# Revit family: DVS
name_source: partatom
category: Wyposażenie mechaniczne
revit_build: Autodesk Revit 2017 (Build: 20160225_1515(x64)
units: mm (PartAtom-declared; Revit-internal decimal feet)

## family parameters
Oparty na płaszczyźnie roboczej = Nie
Punkt obliczania pomieszczeń = Nie
Tnij formami wycięć po wczytaniu = Nie
Typ części = Normalny
Współdzielony = Nie
Wymiar okrągłego złącza = Użyj średnicy
Zawsze pionowo = Tak

## types (32) — shared parameters
Date = 01.2019
Frequency = 50 Hz
Producent = Rosenberg
Text_1 = 340 mm
Text_2 = 170 mm
URL = https://www.rosenberg.pl
Version = 1

## per-type parameters (varying)
| type | A | Air_flow | Current | Da | Di | H | Height | L | P | Power | Pressure | Protection_class | Text_size | Voltage | Weight[kg] | Width | Width_bottom | max.Ambient_temperature | t1 |
| 190-2 E.3BE | 294 mm  [stored 0.964567 ft] | 291.0 m³/h | 0 A | 235 mm  [stored 0.770997 ft] | 186 mm  [stored 0.610236 ft] | 600 mm | 290 mm  [stored 0.951444 ft] | 115 mm  [stored 0.377297 ft] | 571 mm  [stored 1.87336 ft] | 0 kW | 199.0 Pa | IP44 | 15 mm  [stored 0.0492126 ft] | 230 V | 22 | 540 mm  [stored 1.77165 ft] | 335 mm  [stored 1.09908 ft] | 70 °C | 2 mm  [stored 0.00656168 ft] |
| 225-2 E.3CF | 294 mm  [stored 0.964567 ft] | 449.0 m³/h | 0 A | 235 mm  [stored 0.770997 ft] | 186 mm  [stored 0.610236 ft] | 600 mm | 290 mm  [stored 0.951444 ft] | 115 mm  [stored 0.377297 ft] | 571 mm  [stored 1.87336 ft] | 0 kW | 218.0 Pa | IP44 | 20 mm  [stored 0.0656168 ft] | 230 V | 9 | 540 mm  [stored 1.77165 ft] | 335 mm  [stored 1.09908 ft] | 70 °C | 2 mm  [stored 0.00656168 ft] |
| 280-2 E.3EF V1 | 395 mm  [stored 1.29593 ft] | 839.0 m³/h | 1 A | 306 mm  [stored 1.00394 ft] | 256 mm  [stored 0.839895 ft] | 700 mm | 390 mm  [stored 1.27953 ft] | 156 mm  [stored 0.511811 ft] | 657 mm | 0 kW | 381.0 Pa | IP44 | 25 mm  [stored 0.082021 ft] | 230 V | 22.5 | 720 mm | 435 mm  [stored 1.42717 ft] | 70 °C | 2 mm  [stored 0.00656168 ft] |
| 310-4 E.3EF | 395 mm  [stored 1.29593 ft] | 1031.0 m³/h | 1 A | 306 mm  [stored 1.00394 ft] | 256 mm  [stored 0.839895 ft] | 700 mm | 390 mm  [stored 1.27953 ft] | 156 mm  [stored 0.511811 ft] | 657 mm | 0 kW | 133.0 Pa | IP44 | 25 mm  [stored 0.082021 ft] | 230 V | 22 | 720 mm | 435 mm  [stored 1.42717 ft] | 70 °C | 2 mm  [stored 0.00656168 ft] |
| 355-4 E.5FA | 555 mm  [stored 1.82087 ft] | 1639.0 m³/h | 1 A | 464 mm  [stored 1.52231 ft] | 402 mm  [stored 1.3189 ft] | 900 mm | 445 mm  [stored 1.45997 ft] | 220 mm  [stored 0.721785 ft] | 817 mm | 0 kW | 278.0 Pa | IP54 | 30 mm  [stored 0.0984252 ft] | 230 V | 34 | 915 mm | 595 mm  [stored 1.9521 ft] | 70 °C | 2 mm  [stored 0.00656168 ft] |
| 400-4 E.5HA | 555 mm  [stored 1.82087 ft] | 2411.0 m³/h | 3 A | 464 mm  [stored 1.52231 ft] | 402 mm  [stored 1.3189 ft] | 900 mm | 445 mm  [stored 1.45997 ft] | 220 mm  [stored 0.721785 ft] | 817 mm | 1 kW | 330.0 Pa | IP54 | 35 mm  [stored 0.114829 ft] | 230 V | 34 | 915 mm | 595 mm  [stored 1.9521 ft] | 65 °C | 2 mm  [stored 0.00656168 ft] |
| 450-4 E.6FA | 625 mm | 3424.0 m³/h | 4 A | 464 mm  [stored 1.52231 ft] | 402 mm  [stored 1.3189 ft] | 900 mm | 480 mm  [stored 1.5748 ft] | 220 mm  [stored 0.721785 ft] | 877 mm | 1 kW | 448.0 Pa | IP54 | 40 mm  [stored 0.131234 ft] | 230 V | 46.2 | 1005 mm | 665 mm | 45 °C | 2 mm  [stored 0.00656168 ft] |
| 500-4 E.6HF | 625 mm | 4745.0 m³/h | 6 A | 464 mm  [stored 1.52231 ft] | 402 mm  [stored 1.3189 ft] | 900 mm | 480 mm  [stored 1.5748 ft] | 220 mm  [stored 0.721785 ft] | 877 mm | 1 kW | 509.0 Pa | IP54 | 50 mm  [stored 0.164042 ft] | 230 V | 54 | 1005 mm | 665 mm | 40 °C | 2 mm  [stored 0.00656168 ft] |
| 560-4 D Zone 1 | 895 mm | 0.0 m³/h | 5 A | 639 mm | 569 mm  [stored 1.8668 ft] | 1070 mm | 520 mm  [stored 1.70604 ft] | 255 mm  [stored 0.836614 ft] | 1200 mm | 2 kW | 0.0 Pa | IP44 | 50 mm  [stored 0.164042 ft] | 400 V | 68 | 1150 mm | 939 mm | 40 °C | 2 mm  [stored 0.00656168 ft] |
| 630-4 D.7KF | 895 mm | 9404.0 m³/h | 6 A | 639 mm | 569 mm  [stored 1.8668 ft] | 1070 mm | 600 mm | 255 mm  [stored 0.836614 ft] | 1200 mm | 4 kW | 718.0 Pa | IP54 | 50 mm  [stored 0.164042 ft] | 400 V | 94 | 1405 mm | 939 mm | 40 °C | 2 mm  [stored 0.00656168 ft] |
| 710-6 D.7NA | 985 mm | 8203.0 m³/h | 5 A | 708 mm | 635 mm | 1160 mm | 700 mm | 250 mm  [stored 0.82021 ft] | 1300 mm | 2 kW | 479.0 Pa | IP54 | 50 mm  [stored 0.164042 ft] | 400 V | 115 | 1510 mm | 1035 mm | 70 °C | 4 mm  [stored 0.0131234 ft] |
| 280-4 E.3EF | 395 mm  [stored 1.29593 ft] | 674.0 m³/h | 0 A | 306 mm  [stored 1.00394 ft] | 256 mm  [stored 0.839895 ft] | 700 mm | 390 mm  [stored 1.27953 ft] | 156 mm  [stored 0.511811 ft] | 657 mm | 0 kW | 129.0 Pa | IP44 | 25 mm  [stored 0.082021 ft] | 230 V | 9.5 | 720 mm | 435 mm  [stored 1.42717 ft] | 70 °C | 2 mm  [stored 0.00656168 ft] |
| 310-4 D.3EF | 395 mm  [stored 1.29593 ft] | 929.0 m³/h | 0 A | 306 mm  [stored 1.00394 ft] | 256 mm  [stored 0.839895 ft] | 700 mm | 390 mm  [stored 1.27953 ft] | 156 mm  [stored 0.511811 ft] | 657 mm | 0 kW | 117.0 Pa | IP54 | 25 mm  [stored 0.082021 ft] | 400 V | 22 | 720 mm | 435 mm  [stored 1.42717 ft] | 70 °C | 2 mm  [stored 0.00656168 ft] |
| 355-4 D.5DF | 555 mm  [stored 1.82087 ft] | 1693.0 m³/h | 1 A | 464 mm  [stored 1.52231 ft] | 402 mm  [stored 1.3189 ft] | 900 mm | 445 mm  [stored 1.45997 ft] | 220 mm  [stored 0.721785 ft] | 817 mm | 0 kW | 266.0 Pa | IP54 | 30 mm  [stored 0.0984252 ft] | 230 V | 25 | 915 mm | 595 mm  [stored 1.9521 ft] | 70 °C | 2 mm  [stored 0.00656168 ft] |
| 400-4 D.5FA | 555 mm  [stored 1.82087 ft] | 2470.0 m³/h | 1 A | 464 mm  [stored 1.52231 ft] | 402 mm  [stored 1.3189 ft] | 900 mm | 445 mm  [stored 1.45997 ft] | 220 mm  [stored 0.721785 ft] | 817 mm | 0 kW | 299.0 Pa | IP54 | 35 mm  [stored 0.114829 ft] | 400 V | 32 | 915 mm | 595 mm  [stored 1.9521 ft] | 70 °C | 2 mm  [stored 0.00656168 ft] |
| 450-4 D.5HA | 625 mm | 3385.0 m³/h | 2 A | 464 mm  [stored 1.52231 ft] | 402 mm  [stored 1.3189 ft] | 900 mm | 480 mm  [stored 1.5748 ft] | 220 mm  [stored 0.721785 ft] | 877 mm | 1 kW | 393.0 Pa | IP54 | 40 mm  [stored 0.131234 ft] | 400 V | 43.5 | 1005 mm | 665 mm | 55 °C | 2 mm  [stored 0.00656168 ft] |
| 450-6 D.5HA | 625 mm | 2289.0 m³/h | 1 A | 464 mm  [stored 1.52231 ft] | 402 mm  [stored 1.3189 ft] | 900 mm | 480 mm  [stored 1.5748 ft] | 220 mm  [stored 0.721785 ft] | 877 mm | 0 kW | 178.0 Pa | IP54 | 40 mm  [stored 0.131234 ft] | 400 V | 43.5 | 1005 mm | 665 mm | 60 °C | 2 mm  [stored 0.00656168 ft] |
| 500-4 D.6HF | 625 mm | 4635.0 m³/h | 3 A | 464 mm  [stored 1.52231 ft] | 402 mm  [stored 1.3189 ft] | 900 mm | 480 mm  [stored 1.5748 ft] | 220 mm  [stored 0.721785 ft] | 877 mm | 1 kW | 527.0 Pa | IP54 | 50 mm  [stored 0.164042 ft] | 400 V | 53 | 1005 mm | 665 mm | 70 °C | 2 mm  [stored 0.00656168 ft] |
| 500-6 D.6DF | 625 mm | 3114.0 m³/h | 1 A | 464 mm  [stored 1.52231 ft] | 402 mm  [stored 1.3189 ft] | 900 mm | 480 mm  [stored 1.5748 ft] | 220 mm  [stored 0.721785 ft] | 877 mm | 0 kW | 221.0 Pa | IP54 | 50 mm  [stored 0.164042 ft] | 400 V | 53 | 1005 mm | 665 mm | 65 °C | 2 mm  [stored 0.00656168 ft] |
| 560-6 D.6FA | 895 mm | 4452.0 m³/h | 2 A | 639 mm | 569 mm  [stored 1.8668 ft] | 1070 mm | 600 mm | 255 mm  [stored 0.836614 ft] | 1200 mm | 1 kW | 267.0 Pa | IP54 | 50 mm  [stored 0.164042 ft] | 400 V | 77 | 1405 mm | 939 mm | 50 °C | 2 mm  [stored 0.00656168 ft] |
| 630-6 D.6LA | 895 mm | 5181.0 m³/h | 3 A | 639 mm | 569 mm  [stored 1.8668 ft] | 1070 mm | 600 mm | 255 mm  [stored 0.836614 ft] | 1200 mm | 1 kW | 418.0 Pa | IP54 | 50 mm  [stored 0.164042 ft] | 400 V | 83 | 1405 mm | 939 mm | 65 °C | 2 mm  [stored 0.00656168 ft] |
| 800-6 KD.7NA | 985 mm | 10571.0 m³/h | 6 A | 708 mm | 635 mm | 1160 mm | 700 mm | 250 mm  [stored 0.82021 ft] | 1300 mm | 3 kW | 572.0 Pa | IP54 | 50 mm  [stored 0.164042 ft] | 400 V | 172 | 1510 mm | 1035 mm | 50 °C | 4 mm  [stored 0.0131234 ft] |
| 310 K-4 D Zone 2 | 395 mm  [stored 1.29593 ft] | 0.0 m³/h | 0 A | 306 mm  [stored 1.00394 ft] | 256 mm  [stored 0.839895 ft] | 700 mm | 350 mm  [stored 1.14829 ft] | 156 mm  [stored 0.511811 ft] | 657 mm | 0 kW | 0.0 Pa | IP44 | 25 mm  [stored 0.082021 ft] | 400 V | 22 | 560 mm  [stored 1.83727 ft] | 435 mm  [stored 1.42717 ft] | 40 °C | 2 mm  [stored 0.00656168 ft] |
| 310 L-4 D Zone 2 | 395 mm  [stored 1.29593 ft] | 0.0 m³/h | 0 A | 306 mm  [stored 1.00394 ft] | 256 mm  [stored 0.839895 ft] | 700 mm | 350 mm  [stored 1.14829 ft] | 156 mm  [stored 0.511811 ft] | 657 mm | 0 kW | 0.0 Pa | IP44 | 25 mm  [stored 0.082021 ft] | 400 V | 21.5 | 560 mm  [stored 1.83727 ft] | 435 mm  [stored 1.42717 ft] | 40 °C | 2 mm  [stored 0.00656168 ft] |
| 355-4 D Zone 1 | 555 mm  [stored 1.82087 ft] | 0.0 m³/h | 1 A | 464 mm  [stored 1.52231 ft] | 402 mm  [stored 1.3189 ft] | 900 mm | 445 mm  [stored 1.45997 ft] | 220 mm  [stored 0.721785 ft] | 817 mm | 0 kW | 0.0 Pa | IP44 | 30 mm  [stored 0.0984252 ft] | 400 V | 32 | 915 mm | 595 mm  [stored 1.9521 ft] | 40 °C | 2 mm  [stored 0.00656168 ft] |
| 355-4 D Zone 2 | 555 mm  [stored 1.82087 ft] | 0.0 m³/h | 1 A | 464 mm  [stored 1.52231 ft] | 402 mm  [stored 1.3189 ft] | 900 mm | 445 mm  [stored 1.45997 ft] | 220 mm  [stored 0.721785 ft] | 817 mm | 0 kW | 0.0 Pa | IP44 | 30 mm  [stored 0.0984252 ft] | 400 V | 32 | 915 mm | 595 mm  [stored 1.9521 ft] | 40 °C | 2 mm  [stored 0.00656168 ft] |
| 400-4 D Zone 2 | 555 mm  [stored 1.82087 ft] | 0.0 m³/h | 1 A | 464 mm  [stored 1.52231 ft] | 402 mm  [stored 1.3189 ft] | 900 mm | 445 mm  [stored 1.45997 ft] | 220 mm  [stored 0.721785 ft] | 817 mm | 0 kW | 0.0 Pa | IP44 | 35 mm  [stored 0.114829 ft] | 400 V | 24.5 | 915 mm | 595 mm  [stored 1.9521 ft] | 40 °C | 2 mm  [stored 0.00656168 ft] |
| 450-4 D Zone 1 | 625 mm | 0.0 m³/h | 1 A | 464 mm  [stored 1.52231 ft] | 402 mm  [stored 1.3189 ft] | 900 mm | 450 mm  [stored 1.47638 ft] | 220 mm  [stored 0.721785 ft] | 877 mm | 1 kW | 0.0 Pa | IP44 | 40 mm  [stored 0.131234 ft] | 400 V | 43.5 | 900 mm | 665 mm | 40 °C | 2 mm  [stored 0.00656168 ft] |
| 450-4 D Zone 2 | 625 mm | 0.0 m³/h | 1 A | 464 mm  [stored 1.52231 ft] | 402 mm  [stored 1.3189 ft] | 900 mm | 450 mm  [stored 1.47638 ft] | 220 mm  [stored 0.721785 ft] | 877 mm | 1 kW | 0.0 Pa | IP44 | 40 mm  [stored 0.131234 ft] | 400 V | 41.5 | 900 mm | 665 mm | 40 °C | 2 mm  [stored 0.00656168 ft] |
| 500-4 D Zone 1 | 625 mm | 0.0 m³/h | 3 A | 464 mm  [stored 1.52231 ft] | 402 mm  [stored 1.3189 ft] | 900 mm | 450 mm  [stored 1.47638 ft] | 220 mm  [stored 0.721785 ft] | 877 mm | 1 kW | 0.0 Pa | IP44 | 50 mm  [stored 0.164042 ft] | 400 V | 50 | 900 mm | 665 mm | 40 °C | 2 mm  [stored 0.00656168 ft] |
| 560-4 D Zone 2 | 895 mm | 0.0 m³/h | 5 A | 639 mm | 569 mm  [stored 1.8668 ft] | 1070 mm | 520 mm  [stored 1.70604 ft] | 255 mm  [stored 0.836614 ft] | 1200 mm | 2 kW | 0.0 Pa | IP44 | 50 mm  [stored 0.164042 ft] | 400 V | 68 | 1150 mm | 939 mm | 40 °C | 2 mm  [stored 0.00656168 ft] |
| 560-4 D.6LA | 895 mm | 6725.0 m³/h | 4 A | 639 mm | 569 mm  [stored 1.8668 ft] | 1070 mm | 600 mm | 255 mm  [stored 0.836614 ft] | 1200 mm | 2 kW | 610.0 Pa | IP54 | 50 mm  [stored 0.164042 ft] | 400 V | 77 | 1405 mm | 939 mm | 50 °C | 2 mm  [stored 0.00656168 ft] |

note: column(s) folded — value = type name in every type: Model

note: [stored X ft] marks values corroborated as IEEE doubles in the binary element streams (Revit-internal decimal feet)
